# Revit family: axor_montreux_3_hole_basin_mixer_16534000
name_source: partatom
category: Plumbing Fixtures
revit_build: Autodesk Revit 2015 (Build: 20140903_1530(x64)
units: mm (PartAtom-declared; Revit-internal decimal feet)

## types (2) — shared parameters
BIMobject category = Taps & Mixers
BOSUseNativeGeometries = 1
Brand url = http://www.hansgrohe-int.com
Default Elevation = 4' - 0"
Design country = Germany
EAN code = https://4011097785028
Edition number = 1
IFC Classification = Sanitary Terminal
Installation instructions = https://pro.hansgrohe-int.com
Manufacturer country = Germany
Manufacturer name = AXOR
Masterformat 2014 Code = 01 52 19
Masterformat 2014 Description = Sanitary Facilities
Material main = Chrome
NBS Reference Code = 31-76
NBS Reference Description = Sanitary Dispensing And Disposal Units
OmniClass Code = 23-31 11 00
OmniClass Description = Faucets
Product Guid = 3169fde0-9286-4915-83ab-4eaa4db7e8de
Product SKU = 16534000
Product data url = https://bimobject.com
Product family = AXOR Montreux
Product group = Basin mixers
Product url = https://pro.hansgrohe-int.com
QR code = http://bimobject.com
Technical description = https://pro.hansgrohe-int.com
UNSPSC Code = 301815
Uniclass 1.4 Code = L721
Uniclass 1.4 Description = Sanitary equipment
Uniclass 2.0 Code = PR-31-76
Uniclass 2.0 Description = Sanitary Dispensing And Disposal Units
Uniclass 2015 Code = Pr_40_20
Uniclass 2015 Name = Sanitary fittings and accessories
Uniformat II Code = D2010
Uniformat II Description = Plumbing Fixtures
zero-valued in all types: Nominal height, Nominal width, Weight Net (Kg)

## type names (no varying parameters)
- Default
- Chrome 000

## geometry (parser evidence)
native form markers: Sweep x2
no freeform markers — native parametric forms only
